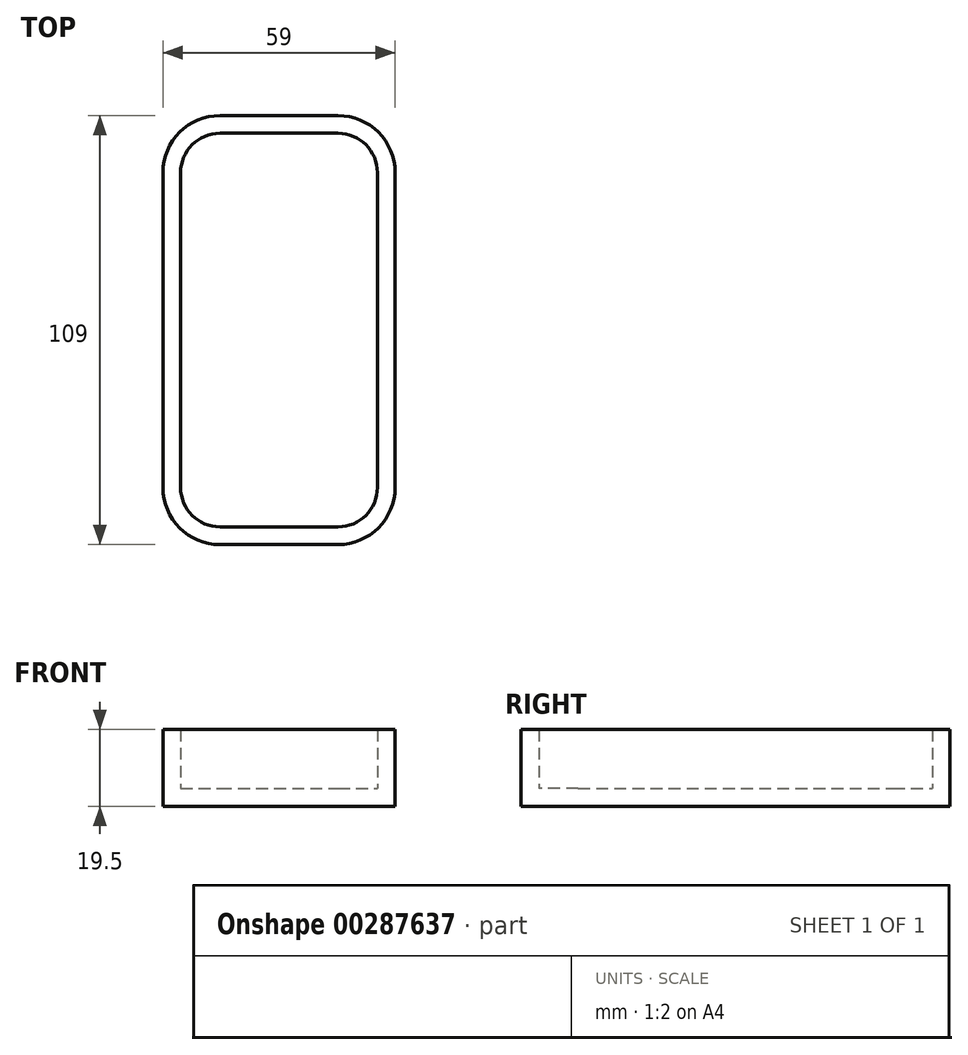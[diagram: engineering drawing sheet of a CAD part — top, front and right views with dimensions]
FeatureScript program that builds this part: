
annotation { "Feature Type Name" : "Feature", "Feature Type Description" : "" }
export const myFeature = defineFeature(function(context is Context, id is Id, definition is map)
    precondition{}
    {
        {
            var Q0;
            Q0=qCreatedBy(makeId("Top.planeOp"),FACE);
            var sketch = newSketch(context, id + "F0", { "sketchPlane" : qUnion([Q0])});
            skLineSegment(sketch, "E0.bottom", {"start": v(0, 0) * mm, "end": v(50, 0) * mm});
            skLineSegment(sketch, "E0.top", {"start": v(0, 100) * mm, "end": v(50, 100) * mm});
            skLineSegment(sketch, "E0.left", {"start": v(0, 0) * mm, "end": v(0, 100) * mm});
            skLineSegment(sketch, "E0.right", {"start": v(50, 0) * mm, "end": v(50, 100) * mm});
            skSolve(sketch);
        }
        {
            var Q0;
            Q0=makeQuery(id+"F0.imprint","IMPRINT",FACE,{"disambiguationData":[TD([[makeQuery(id+"F0.imprint","IMPRINT",EDGE,{"derivedFrom":sQuery(id+"F0.wireOp",EDGE,"E0.bottom")}),1.0]])]});
            extrude(context, id + "F1", {"entities" : qUnion([Q0]), "depth" : 15 * mm});
        }
        {
            var Q0;
            Q0=makeQuery(id+"F1.opExtrude","SWEPT_EDGE",EDGE,{"disambiguationData":[OSD([sQuery(id+"F0.wireOp",EDGE,"E0.bottom"),sQuery(id+"F0.wireOp",EDGE,"E0.left")])]});
            var Q1;
            Q1=makeQuery(id+"F1.opExtrude","SWEPT_EDGE",EDGE,{"disambiguationData":[OSD([sQuery(id+"F0.wireOp",EDGE,"E0.bottom"),sQuery(id+"F0.wireOp",EDGE,"E0.right")])]});
            var Q2;
            Q2=makeQuery(id+"F1.opExtrude","SWEPT_EDGE",EDGE,{"disambiguationData":[OSD([sQuery(id+"F0.wireOp",EDGE,"E0.top"),sQuery(id+"F0.wireOp",EDGE,"E0.right")])]});
            var Q3;
            Q3=makeQuery(id+"F1.opExtrude","SWEPT_EDGE",EDGE,{"disambiguationData":[OSD([sQuery(id+"F0.wireOp",EDGE,"E0.top"),sQuery(id+"F0.wireOp",EDGE,"E0.left")])]});
            fillet(context, id + "F2", {"entities" : qUnion([Q0, Q1, Q2, Q3]), "radius" : 10 * mm, "tangentPropagation" : true, "allowEdgeOverflow" : false});
        }
        {
            var Q0;
            Q0=makeQuery(id+"F1.opExtrude","CAP_FACE",FACE,{"disambiguationData":[OSD([sQuery(id+"F0.wireOp",EDGE,"E0.bottom"),sQuery(id+"F0.wireOp",EDGE,"E0.top"),sQuery(id+"F0.wireOp",EDGE,"E0.left"),sQuery(id+"F0.wireOp",EDGE,"E0.right")])],"isStart":false});
            shell(context, id + "F3", {"entities" : qUnion([Q0]), "thickness" : 4.5 * mm, "oppositeDirection" : true});
        }
    });
